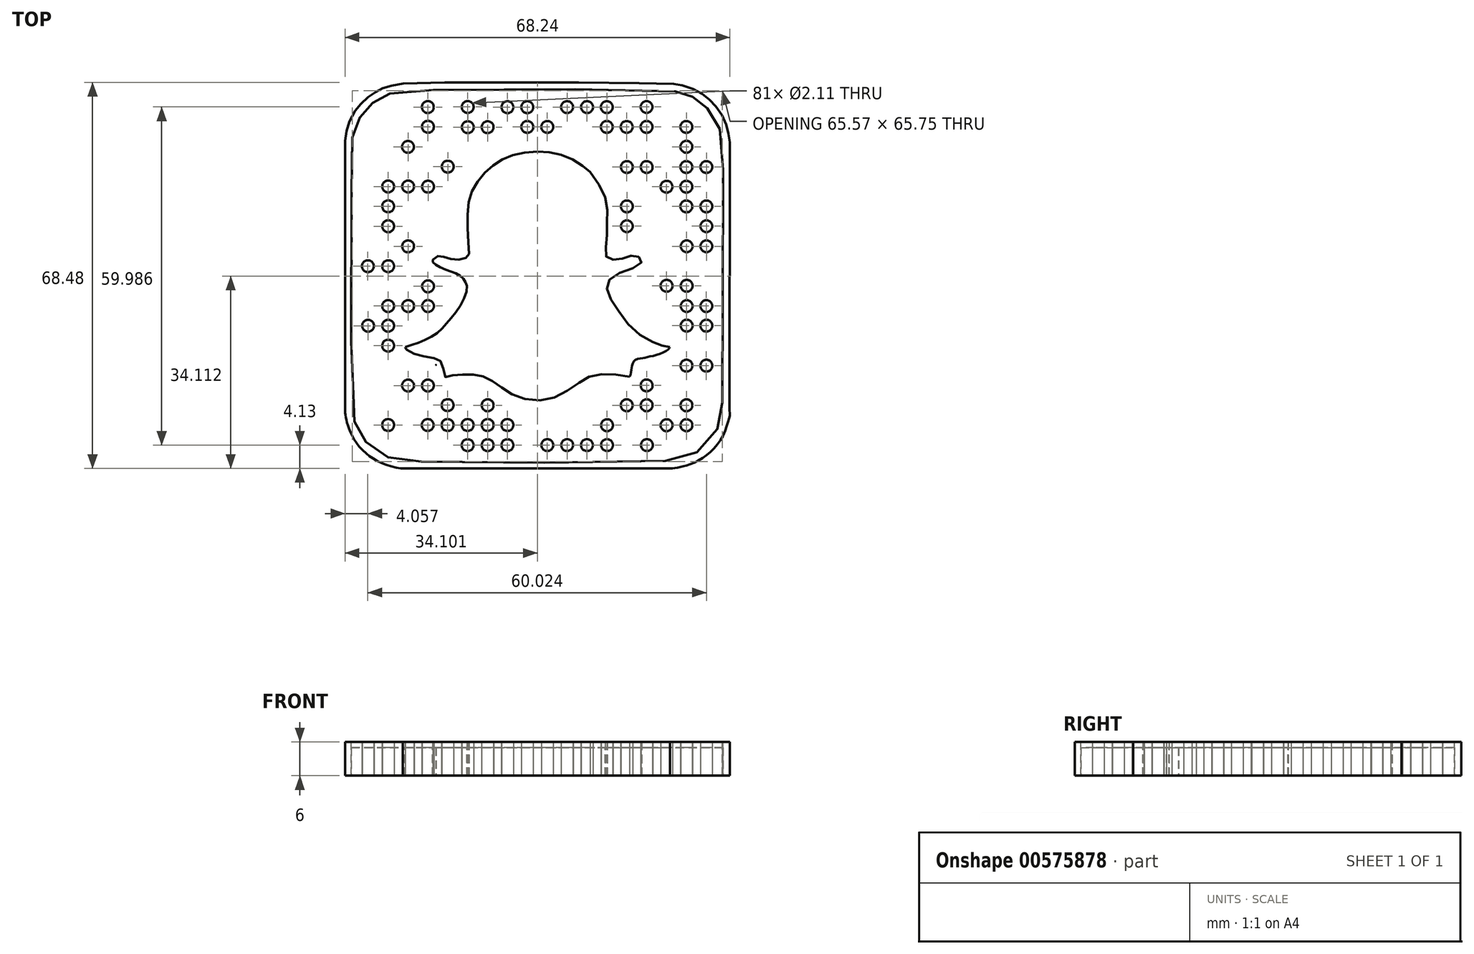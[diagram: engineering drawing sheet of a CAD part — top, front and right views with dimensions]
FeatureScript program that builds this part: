
annotation { "Feature Type Name" : "Feature", "Feature Type Description" : "" }
export const myFeature = defineFeature(function(context is Context, id is Id, definition is map)
    precondition{}
    {
        {
            var Q0;
            Q0=qCreatedBy(makeId("Top.planeOp"),FACE);
            var sketch = newSketch(context, id + "F0", { "sketchPlane" : qUnion([Q0])});
            skFitSpline(sketch, "E0", {"points": [v(0, 58.1) * mm, v(0, 10.12) * mm], "startDerivative": vector(0, -47.98) * mm, "endDerivative": vector(0, -47.98) * mm});
            skFitSpline(sketch, "E1", {"points": [v(0, 10.12) * mm, v(0.05, 9.95) * mm, v(0.07, 9.75) * mm, v(0.11, 9.43) * mm, v(0.2, 8.84) * mm, v(0.3, 8.4) * mm, v(0.46, 7.77) * mm, v(0.7, 7.06) * mm, v(1.15, 6.01) * mm, v(1.79, 4.9) * mm, v(2.7, 3.68) * mm, v(4, 2.48) * mm, v(4.96, 1.76) * mm, v(6.58, 0.92) * mm, v(8.37, 0.3) * mm, v(9.94, 0) * mm, v(10.25, 0) * mm], "startDerivative": vector(2.05, -5.87) * mm, "endDerivative": vector(6.58, 0.5) * mm});
            skFitSpline(sketch, "E2", {"points": [v(10.25, 0) * mm, v(57.62, 0) * mm], "startDerivative": vector(47.37, 0) * mm, "endDerivative": vector(47.37, 0) * mm});
            skFitSpline(sketch, "E3", {"points": [v(57.62, 0) * mm, v(58.24, 0) * mm, v(59.04, 0.17) * mm, v(59.98, 0.37) * mm, v(61.45, 0.82) * mm, v(63.58, 1.94) * mm, v(65.65, 3.77) * mm, v(67.27, 6.33) * mm, v(68, 8.6) * mm, v(68.24, 9.47) * mm, v(68.18, 10.3) * mm], "startDerivative": vector(9.32, -0.59) * mm, "endDerivative": vector(-1.36, 11.59) * mm});
            skFitSpline(sketch, "E4", {"points": [v(68.18, 10.3) * mm, v(68.22, 57.82) * mm, v(68.22, 57.86) * mm, v(68.22, 57.86) * mm], "startDerivative": vector(0.05, 72.45) * mm, "endDerivative": vector(0, 0.4) * mm});
            skFitSpline(sketch, "E5", {"points": [v(68.22, 57.86) * mm, v(68.04, 59.12) * mm, v(67.79, 60.34) * mm, v(67.15, 61.98) * mm, v(66.32, 63.49) * mm, v(65.2, 64.83) * mm, v(64.27, 65.75) * mm, v(63, 66.64) * mm, v(61.26, 67.48) * mm, v(59.55, 68.04) * mm, v(57.88, 68.22) * mm, v(9.78, 68.22) * mm, v(8.28, 67.9) * mm, v(6.86, 67.45) * mm, v(5.86, 66.99) * mm, v(4.83, 66.38) * mm, v(3.63, 65.49) * mm, v(2.59, 64.32) * mm, v(1.77, 63.32) * mm, v(0.67, 61.16) * mm, v(0.24, 59.69) * mm, v(0, 58.1) * mm], "startDerivative": vector(-5.16, 36.2) * mm, "endDerivative": vector(-5.3, -41.25) * mm});
            skFitSpline(sketch, "E6", {"points": [v(1.31, 58.65) * mm, v(1.3, 58.4) * mm, v(1.28, 58.1) * mm, v(1.42, 9.95) * mm, v(1.9, 7.9) * mm, v(2.76, 6.03) * mm, v(4.25, 4.07) * mm, v(6.21, 2.62) * mm, v(8.79, 1.5) * mm, v(11.56, 1.22) * mm, v(58.24, 1.44) * mm, v(61.22, 2.24) * mm, v(63.68, 3.77) * mm, v(65.85, 6.61) * mm, v(66.79, 9.3) * mm, v(66.89, 12.9) * mm, v(66.9, 57.86) * mm, v(66.64, 59.59) * mm, v(65.99, 61.46) * mm, v(64.89, 63.22) * mm, v(63.63, 64.5) * mm, v(63.04, 65.05) * mm, v(61.92, 65.75) * mm, v(60.43, 66.36) * mm, v(59.5, 66.63) * mm, v(57.98, 66.9) * mm, v(9.78, 66.93) * mm, v(8.5, 66.65) * mm, v(7.27, 66.2) * mm, v(5.9, 65.52) * mm, v(4.99, 64.9) * mm, v(4.16, 64.13) * mm, v(3.24, 63.17) * mm, v(2.3, 61.6) * mm, v(1.57, 59.77) * mm, v(1.31, 58.65) * mm]});
            skCircle(sketch, "E7", {"center": v(11.18, 57.03) * mm, "radius": 1.05 * mm});
            skCircle(sketch, "E8", {"center": v(14.71, 60.59) * mm, "radius": 1.05 * mm});
            skCircle(sketch, "E9", {"center": v(21.76, 64.1) * mm, "radius": 1.05 * mm});
            skCircle(sketch, "E10", {"center": v(21.79, 60.52) * mm, "radius": 1.05 * mm});
            skCircle(sketch, "E11", {"center": v(18.23, 53.52) * mm, "radius": 1.05 * mm});
            skCircle(sketch, "E12", {"center": v(14.74, 49.97) * mm, "radius": 1.05 * mm});
            skCircle(sketch, "E13", {"center": v(11.2, 50) * mm, "radius": 1.05 * mm});
            skCircle(sketch, "E14", {"center": v(14.7, 64.09) * mm, "radius": 1.05 * mm});
            skCircle(sketch, "E15", {"center": v(7.67, 46.48) * mm, "radius": 1.05 * mm});
            skCircle(sketch, "E16", {"center": v(7.67, 42.94) * mm, "radius": 1.05 * mm});
            skCircle(sketch, "E17", {"center": v(11.2, 39.38) * mm, "radius": 1.05 * mm});
            skCircle(sketch, "E18", {"center": v(7.67, 35.86) * mm, "radius": 1.05 * mm});
            skCircle(sketch, "E19", {"center": v(4.06, 35.86) * mm, "radius": 1.05 * mm});
            skCircle(sketch, "E20", {"center": v(7.67, 28.8) * mm, "radius": 1.05 * mm});
            skCircle(sketch, "E21", {"center": v(7.67, 25.3) * mm, "radius": 1.05 * mm});
            skCircle(sketch, "E22", {"center": v(7.67, 21.77) * mm, "radius": 1.05 * mm});
            skCircle(sketch, "E23", {"center": v(4.1, 25.3) * mm, "radius": 1.05 * mm});
            skCircle(sketch, "E24", {"center": v(14.73, 32.3) * mm, "radius": 1.05 * mm});
            skCircle(sketch, "E25", {"center": v(11.2, 28.8) * mm, "radius": 1.05 * mm});
            skCircle(sketch, "E26", {"center": v(14.73, 28.8) * mm, "radius": 1.05 * mm});
            skCircle(sketch, "E27", {"center": v(7.67, 50) * mm, "radius": 1.05 * mm});
            skCircle(sketch, "E28", {"center": v(14.68, 7.7) * mm, "radius": 1.05 * mm});
            skCircle(sketch, "E29", {"center": v(18.2, 7.7) * mm, "radius": 1.05 * mm});
            skCircle(sketch, "E30", {"center": v(25.3, 11.19) * mm, "radius": 1.05 * mm});
            skCircle(sketch, "E31", {"center": v(28.8, 7.7) * mm, "radius": 1.05 * mm});
            skCircle(sketch, "E32", {"center": v(25.3, 7.7) * mm, "radius": 1.05 * mm});
            skCircle(sketch, "E33", {"center": v(25.3, 4.12) * mm, "radius": 1.05 * mm});
            skCircle(sketch, "E34", {"center": v(18.2, 11.22) * mm, "radius": 1.05 * mm});
            skCircle(sketch, "E35", {"center": v(14.71, 14.7) * mm, "radius": 1.05 * mm});
            skCircle(sketch, "E36", {"center": v(11.2, 14.7) * mm, "radius": 1.05 * mm});
            skCircle(sketch, "E37", {"center": v(7.66, 7.7) * mm, "radius": 1.05 * mm});
            skCircle(sketch, "E38", {"center": v(21.75, 7.7) * mm, "radius": 1.05 * mm});
            skCircle(sketch, "E39", {"center": v(21.75, 4.12) * mm, "radius": 1.05 * mm});
            skCircle(sketch, "E40", {"center": v(46.46, 7.66) * mm, "radius": 1.05 * mm});
            skCircle(sketch, "E41", {"center": v(35.88, 4.13) * mm, "radius": 1.05 * mm});
            skCircle(sketch, "E42", {"center": v(28.8, 4.12) * mm, "radius": 1.05 * mm});
            skCircle(sketch, "E43", {"center": v(53.53, 4.13) * mm, "radius": 1.05 * mm});
            skCircle(sketch, "E44", {"center": v(42.9, 4.13) * mm, "radius": 1.05 * mm});
            skCircle(sketch, "E45", {"center": v(39.4, 4.13) * mm, "radius": 1.05 * mm});
            skCircle(sketch, "E46", {"center": v(46.46, 4.13) * mm, "radius": 1.05 * mm});
            skCircle(sketch, "E47", {"center": v(57.01, 7.66) * mm, "radius": 1.05 * mm});
            skCircle(sketch, "E48", {"center": v(53.48, 11.19) * mm, "radius": 1.05 * mm});
            skCircle(sketch, "E49", {"center": v(49.95, 11.19) * mm, "radius": 1.05 * mm});
            skCircle(sketch, "E50", {"center": v(64.07, 28.8) * mm, "radius": 1.05 * mm});
            skCircle(sketch, "E51", {"center": v(60.54, 18.22) * mm, "radius": 1.05 * mm});
            skCircle(sketch, "E52", {"center": v(64.06, 25.32) * mm, "radius": 1.05 * mm});
            skCircle(sketch, "E53", {"center": v(53.48, 14.72) * mm, "radius": 1.05 * mm});
            skCircle(sketch, "E54", {"center": v(60.54, 11.19) * mm, "radius": 1.05 * mm});
            skCircle(sketch, "E55", {"center": v(60.54, 7.66) * mm, "radius": 1.05 * mm});
            skCircle(sketch, "E56", {"center": v(60.58, 25.32) * mm, "radius": 1.05 * mm});
            skCircle(sketch, "E57", {"center": v(60.58, 28.8) * mm, "radius": 1.05 * mm});
            skCircle(sketch, "E58", {"center": v(64.06, 18.22) * mm, "radius": 1.05 * mm});
            skCircle(sketch, "E59", {"center": v(49.98, 46.46) * mm, "radius": 1.05 * mm});
            skCircle(sketch, "E60", {"center": v(60.58, 39.4) * mm, "radius": 1.05 * mm});
            skCircle(sketch, "E61", {"center": v(64.07, 39.4) * mm, "radius": 1.05 * mm});
            skCircle(sketch, "E62", {"center": v(57, 32.39) * mm, "radius": 1.05 * mm});
            skCircle(sketch, "E63", {"center": v(64.07, 42.96) * mm, "radius": 1.05 * mm});
            skCircle(sketch, "E64", {"center": v(60.58, 32.39) * mm, "radius": 1.05 * mm});
            skCircle(sketch, "E65", {"center": v(64.07, 46.46) * mm, "radius": 1.05 * mm});
            skCircle(sketch, "E66", {"center": v(60.53, 46.46) * mm, "radius": 1.05 * mm});
            skCircle(sketch, "E67", {"center": v(60.53, 57.04) * mm, "radius": 1.05 * mm});
            skCircle(sketch, "E68", {"center": v(60.53, 49.96) * mm, "radius": 1.05 * mm});
            skCircle(sketch, "E69", {"center": v(57, 49.96) * mm, "radius": 1.05 * mm});
            skCircle(sketch, "E70", {"center": v(60.53, 53.46) * mm, "radius": 1.05 * mm});
            skCircle(sketch, "E71", {"center": v(64.08, 53.46) * mm, "radius": 1.05 * mm});
            skCircle(sketch, "E72", {"center": v(53.5, 53.46) * mm, "radius": 1.05 * mm});
            skCircle(sketch, "E73", {"center": v(49.97, 53.46) * mm, "radius": 1.05 * mm});
            skCircle(sketch, "E74", {"center": v(49.98, 42.96) * mm, "radius": 1.05 * mm});
            skCircle(sketch, "E75", {"center": v(49.94, 60.56) * mm, "radius": 1.05 * mm});
            skCircle(sketch, "E76", {"center": v(53.47, 60.56) * mm, "radius": 1.05 * mm});
            skCircle(sketch, "E77", {"center": v(25.3, 60.52) * mm, "radius": 1.05 * mm});
            skCircle(sketch, "E78", {"center": v(32.34, 64.07) * mm, "radius": 1.05 * mm});
            skCircle(sketch, "E79", {"center": v(39.39, 64.08) * mm, "radius": 1.05 * mm});
            skCircle(sketch, "E80", {"center": v(46.42, 64.08) * mm, "radius": 1.05 * mm});
            skCircle(sketch, "E81", {"center": v(53.47, 64.1) * mm, "radius": 1.05 * mm});
            skCircle(sketch, "E82", {"center": v(46.42, 60.56) * mm, "radius": 1.05 * mm});
            skCircle(sketch, "E83", {"center": v(60.53, 60.56) * mm, "radius": 1.05 * mm});
            skCircle(sketch, "E84", {"center": v(28.8, 64.07) * mm, "radius": 1.05 * mm});
            skCircle(sketch, "E85", {"center": v(35.86, 60.56) * mm, "radius": 1.05 * mm});
            skCircle(sketch, "E86", {"center": v(42.92, 64.08) * mm, "radius": 1.05 * mm});
            skCircle(sketch, "E87", {"center": v(32.34, 60.56) * mm, "radius": 1.05 * mm});
            skFitSpline(sketch, "E88", {"points": [v(20.92, 38.22) * mm, v(20.74, 38.1) * mm, v(20.38, 38.01) * mm, v(19.53, 38.03) * mm, v(18.44, 38.3) * mm, v(17.73, 38.6) * mm, v(17.2, 38.75) * mm, v(16.43, 38.73) * mm, v(15.63, 38.49) * mm, v(15.09, 38.08) * mm, v(14.73, 37.65) * mm, v(14.55, 36.99) * mm, v(14.63, 36.18) * mm, v(15.53, 35.17) * mm, v(17, 34.5) * mm, v(18.57, 33.92) * mm, v(19.8, 33.42) * mm, v(20.47, 32.57) * mm, v(20.4, 31.38) * mm, v(19.8, 30.03) * mm, v(19.04, 28.66) * mm, v(17.54, 26.68) * mm, v(15.96, 25.15) * mm, v(14.12, 23.85) * mm, v(11.92, 22.93) * mm, v(10.85, 22.64) * mm, v(9.98, 22.41) * mm, v(9.5, 21.56) * mm, v(10.03, 20.41) * mm, v(11.46, 19.5) * mm, v(14.4, 18.73) * mm, v(16.12, 18.36) * mm, v(16.12, 18.32) * mm], "startDerivative": vector(-11.87, -10.02) * mm, "endDerivative": vector(-12.88, -22.9) * mm});
            skFitSpline(sketch, "E89", {"points": [v(16.12, 18.36) * mm, v(16.17, 18.29) * mm, v(16.22, 18.18) * mm, v(16.28, 17.97) * mm, v(16.39, 17.54) * mm, v(16.5, 17.06) * mm, v(16.63, 16.15) * mm, v(17.14, 15.44) * mm, v(18.08, 15.07) * mm, v(19.37, 15.35) * mm, v(20.56, 15.67) * mm, v(21.95, 15.65) * mm, v(23.55, 15.48) * mm, v(25.16, 14.84) * mm, v(26.44, 14.14) * mm, v(28.49, 12.72) * mm, v(30.12, 11.79) * mm, v(31.78, 11.26) * mm, v(33.93, 11.03) * mm, v(35.8, 11.14) * mm, v(37.84, 11.72) * mm, v(39.95, 12.8) * mm, v(41.25, 13.84) * mm, v(42.87, 14.75) * mm, v(44.7, 15.55) * mm, v(46.76, 15.62) * mm, v(48.87, 15.43) * mm, v(50.18, 15.24) * mm, v(51.1, 15.46) * mm, v(51.56, 16.38) * mm, v(51.8, 17.28) * mm, v(52.07, 18.35) * mm], "startDerivative": vector(5.86, -7.66) * mm, "endDerivative": vector(9.53, 30.18) * mm});
            skFitSpline(sketch, "E90", {"points": [v(51.97, 18.05) * mm, v(52.07, 18.36) * mm, v(53.1, 18.36) * mm, v(54.9, 18.76) * mm, v(57.23, 19.65) * mm, v(58.5, 20.77) * mm, v(58.77, 21.84) * mm, v(58.36, 22.37) * mm, v(57.52, 22.5) * mm, v(55.9, 23.08) * mm, v(53.74, 24.17) * mm, v(51.97, 25.38) * mm, v(50.52, 26.86) * mm, v(49.02, 28.9) * mm, v(48.12, 30.84) * mm, v(47.7, 31.97) * mm, v(48.2, 33.3) * mm, v(50.39, 34.2) * mm, v(52.57, 35.2) * mm, v(53.68, 36.32) * mm, v(53.5, 37.7) * mm, v(51.97, 38.76) * mm, v(50.41, 38.69) * mm, v(49.17, 38.3) * mm, v(47.85, 37.97) * mm, v(47.3, 38.42) * mm, v(47.38, 38.89) * mm, v(47.5, 46.78) * mm, v(46.64, 49.71) * mm, v(45.1, 52.28) * mm, v(43.08, 54.31) * mm, v(41.28, 55.54) * mm, v(38.35, 56.76) * mm, v(34.35, 57.22) * mm, v(31.46, 57.03) * mm, v(28.86, 56.35) * mm, v(26.5, 55.26) * mm, v(24.33, 53.59) * mm, v(22.3, 51.07) * mm, v(21.1, 48.42) * mm, v(20.76, 46.03) * mm, v(20.66, 42.86) * mm, v(20.78, 40.82) * mm, v(20.92, 38.22) * mm], "startDerivative": vector(-15.83, 66.6) * mm, "endDerivative": vector(5.1, -104.53) * mm});
            skFitSpline(sketch, "E91", {"points": [v(15.57, 36.99) * mm, v(15.57, 36.66) * mm, v(16.07, 36.13) * mm, v(17.82, 35.27) * mm, v(19.53, 34.67) * mm, v(20.72, 33.88) * mm, v(21.36, 33.06) * mm, v(21.63, 31.93) * mm, v(20.4, 28.76) * mm, v(18.25, 25.94) * mm, v(16.28, 23.97) * mm, v(13.6, 22.5) * mm, v(10.68, 21.51) * mm], "startDerivative": vector(-1.53, -9.27) * mm, "endDerivative": vector(-27.35, -8.3) * mm});
            skFitSpline(sketch, "E92", {"points": [v(10.68, 21.51) * mm, v(10.62, 21.47) * mm, v(10.68, 21.3) * mm, v(10.8, 21.14) * mm, v(11.65, 20.59) * mm, v(13.25, 20.05) * mm, v(15.04, 19.62) * mm, v(16.5, 19.42) * mm, v(17.03, 18.85) * mm, v(17.44, 17.86) * mm, v(17.75, 16.23) * mm, v(18.15, 16.3) * mm, v(19.53, 16.53) * mm, v(21.34, 16.66) * mm, v(23.4, 16.6) * mm, v(24.88, 16.18) * mm, v(26.79, 15.1) * mm, v(28.68, 13.7) * mm, v(31.44, 12.44) * mm, v(35.42, 12.14) * mm, v(38.84, 13.4) * mm, v(41.76, 15.35) * mm, v(43.77, 16.4) * mm, v(47.18, 16.68) * mm, v(50.43, 16.23) * mm], "startDerivative": vector(-9.2, -2.53) * mm, "endDerivative": vector(55.28, -9.82) * mm});
            skFitSpline(sketch, "E93", {"points": [v(50.43, 16.23) * mm, v(50.55, 16.43) * mm, v(50.72, 17.27) * mm, v(50.92, 18.28) * mm, v(51.42, 19.21) * mm, v(52.65, 19.54) * mm, v(53.8, 19.78) * mm, v(56, 20.37) * mm, v(57.45, 21.23) * mm, v(57.6, 21.5) * mm], "startDerivative": vector(2.35, 2.89) * mm, "endDerivative": vector(1.23, 4.14) * mm});
            skFitSpline(sketch, "E94", {"points": [v(57.6, 21.5) * mm, v(56.5, 21.74) * mm, v(54.94, 22.24) * mm, v(51.5, 24.28) * mm, v(48.5, 27.93) * mm, v(46.68, 30.92) * mm, v(46.53, 32.77) * mm, v(47.97, 34.37) * mm, v(51.3, 35.6) * mm, v(52.57, 36.6) * mm, v(52.3, 37.35) * mm, v(51.22, 37.81) * mm, v(49.91, 37.43) * mm, v(48.3, 37.05) * mm, v(46.76, 37.16) * mm, v(46.19, 37.86) * mm, v(46.37, 40.12) * mm, v(46.46, 42.85) * mm, v(46.5, 45.88) * mm, v(45.85, 48.87) * mm, v(43.45, 52.55) * mm], "startDerivative": vector(-30.34, 5.9) * mm, "endDerivative": vector(-38.13, 53.23) * mm});
            skFitSpline(sketch, "E95", {"points": [v(43.45, 52.55) * mm, v(42, 53.8) * mm, v(39.4, 55.23) * mm, v(36.64, 56) * mm, v(33.83, 56.2) * mm, v(30.61, 55.8) * mm, v(28.17, 54.93) * mm, v(26.1, 53.65) * mm, v(24.4, 52.02) * mm, v(22.86, 49.84) * mm, v(22, 47.63) * mm, v(21.75, 44.46) * mm, v(21.83, 40.72) * mm, v(21.96, 37.93) * mm, v(21.75, 37.51) * mm, v(21.06, 37.2) * mm, v(19.88, 37) * mm, v(18.7, 37.15) * mm, v(17.6, 37.5) * mm, v(16.97, 37.73) * mm, v(16.13, 37.51) * mm, v(15.57, 36.99) * mm], "startDerivative": vector(-27.46, 26.04) * mm, "endDerivative": vector(-16.2, -19.1) * mm});
            skSolve(sketch);
        }
        {
            var Q0;
            Q0 = qSketchRegion(id + "F0", true);
            extrude(context, id + "F1", {"entities" : qUnion([Q0]), "depth" : 5 * mm, "offsetDistance" : 25 * mm});
        }
        {
            var Q0;
            Q0 = qSketchRegion(id + "F0", true);
            var Q1;
            Q1=makeQuery(id+"F0.imprint","IMPRINT",FACE,{"disambiguationData":[TD([[makeQuery(id+"F0.imprint","IMPRINT",EDGE,{"derivedFrom":sQuery(id+"F0.wireOp",EDGE,"E91")}),1.0]])]});
            extrude(context, id + "F2", {"entities" : qUnion([Q0, Q1]), "operationType" : NewBodyOperationType.ADD, "depth" : 6 * mm, "offsetDistance" : 25 * mm});
        }
        {
            var Q0;
            Q0=makeQuery(id+"F0.imprint","IMPRINT",FACE,{"disambiguationData":[TD([[makeQuery(id+"F0.imprint","IMPRINT",EDGE,{"derivedFrom":sQuery(id+"F0.wireOp",EDGE,"E11")}),1.0]])]});
            var Q1;
            Q1=makeQuery(id+"F0.imprint","IMPRINT",FACE,{"disambiguationData":[TD([[makeQuery(id+"F0.imprint","IMPRINT",EDGE,{"derivedFrom":sQuery(id+"F0.wireOp",EDGE,"E12")}),1.0]])]});
            var Q2;
            Q2=makeQuery(id+"F0.imprint","IMPRINT",FACE,{"disambiguationData":[TD([[makeQuery(id+"F0.imprint","IMPRINT",EDGE,{"derivedFrom":sQuery(id+"F0.wireOp",EDGE,"E13")}),1.0]])]});
            var Q3;
            Q3=makeQuery(id+"F0.imprint","IMPRINT",FACE,{"disambiguationData":[TD([[makeQuery(id+"F0.imprint","IMPRINT",EDGE,{"derivedFrom":sQuery(id+"F0.wireOp",EDGE,"E27")}),1.0]])]});
            var Q4;
            Q4=makeQuery(id+"F0.imprint","IMPRINT",FACE,{"disambiguationData":[TD([[makeQuery(id+"F0.imprint","IMPRINT",EDGE,{"derivedFrom":sQuery(id+"F0.wireOp",EDGE,"E15")}),1.0]])]});
            var Q5;
            Q5=makeQuery(id+"F0.imprint","IMPRINT",FACE,{"disambiguationData":[TD([[makeQuery(id+"F0.imprint","IMPRINT",EDGE,{"derivedFrom":sQuery(id+"F0.wireOp",EDGE,"E16")}),1.0]])]});
            var Q6;
            Q6=makeQuery(id+"F0.imprint","IMPRINT",FACE,{"disambiguationData":[TD([[makeQuery(id+"F0.imprint","IMPRINT",EDGE,{"derivedFrom":sQuery(id+"F0.wireOp",EDGE,"E17")}),1.0]])]});
            var Q7;
            Q7=makeQuery(id+"F0.imprint","IMPRINT",FACE,{"disambiguationData":[TD([[makeQuery(id+"F0.imprint","IMPRINT",EDGE,{"derivedFrom":sQuery(id+"F0.wireOp",EDGE,"E7")}),1.0]])]});
            var Q8;
            Q8=makeQuery(id+"F0.imprint","IMPRINT",FACE,{"disambiguationData":[TD([[makeQuery(id+"F0.imprint","IMPRINT",EDGE,{"derivedFrom":sQuery(id+"F0.wireOp",EDGE,"E8")}),1.0]])]});
            var Q9;
            Q9=makeQuery(id+"F0.imprint","IMPRINT",FACE,{"disambiguationData":[TD([[makeQuery(id+"F0.imprint","IMPRINT",EDGE,{"derivedFrom":sQuery(id+"F0.wireOp",EDGE,"E14")}),1.0]])]});
            var Q10;
            Q10=makeQuery(id+"F0.imprint","IMPRINT",FACE,{"disambiguationData":[TD([[makeQuery(id+"F0.imprint","IMPRINT",EDGE,{"derivedFrom":sQuery(id+"F0.wireOp",EDGE,"E9")}),1.0]])]});
            var Q11;
            Q11=makeQuery(id+"F0.imprint","IMPRINT",FACE,{"disambiguationData":[TD([[makeQuery(id+"F0.imprint","IMPRINT",EDGE,{"derivedFrom":sQuery(id+"F0.wireOp",EDGE,"E10")}),1.0]])]});
            var Q12;
            Q12=makeQuery(id+"F0.imprint","IMPRINT",FACE,{"disambiguationData":[TD([[makeQuery(id+"F0.imprint","IMPRINT",EDGE,{"derivedFrom":sQuery(id+"F0.wireOp",EDGE,"E77")}),1.0]])]});
            var Q13;
            Q13=makeQuery(id+"F0.imprint","IMPRINT",FACE,{"disambiguationData":[TD([[makeQuery(id+"F0.imprint","IMPRINT",EDGE,{"derivedFrom":sQuery(id+"F0.wireOp",EDGE,"E84")}),1.0]])]});
            var Q14;
            Q14=makeQuery(id+"F0.imprint","IMPRINT",FACE,{"disambiguationData":[TD([[makeQuery(id+"F0.imprint","IMPRINT",EDGE,{"derivedFrom":sQuery(id+"F0.wireOp",EDGE,"E78")}),1.0]])]});
            var Q15;
            Q15=makeQuery(id+"F0.imprint","IMPRINT",FACE,{"disambiguationData":[TD([[makeQuery(id+"F0.imprint","IMPRINT",EDGE,{"derivedFrom":sQuery(id+"F0.wireOp",EDGE,"E87")}),1.0]])]});
            var Q16;
            Q16=makeQuery(id+"F0.imprint","IMPRINT",FACE,{"disambiguationData":[TD([[makeQuery(id+"F0.imprint","IMPRINT",EDGE,{"derivedFrom":sQuery(id+"F0.wireOp",EDGE,"E85")}),1.0]])]});
            var Q17;
            Q17=makeQuery(id+"F0.imprint","IMPRINT",FACE,{"disambiguationData":[TD([[makeQuery(id+"F0.imprint","IMPRINT",EDGE,{"derivedFrom":sQuery(id+"F0.wireOp",EDGE,"E79")}),1.0]])]});
            var Q18;
            Q18=makeQuery(id+"F0.imprint","IMPRINT",FACE,{"disambiguationData":[TD([[makeQuery(id+"F0.imprint","IMPRINT",EDGE,{"derivedFrom":sQuery(id+"F0.wireOp",EDGE,"E86")}),1.0]])]});
            var Q19;
            Q19=makeQuery(id+"F0.imprint","IMPRINT",FACE,{"disambiguationData":[TD([[makeQuery(id+"F0.imprint","IMPRINT",EDGE,{"derivedFrom":sQuery(id+"F0.wireOp",EDGE,"E80")}),1.0]])]});
            var Q20;
            Q20=makeQuery(id+"F0.imprint","IMPRINT",FACE,{"disambiguationData":[TD([[makeQuery(id+"F0.imprint","IMPRINT",EDGE,{"derivedFrom":sQuery(id+"F0.wireOp",EDGE,"E82")}),1.0]])]});
            var Q21;
            Q21=makeQuery(id+"F0.imprint","IMPRINT",FACE,{"disambiguationData":[TD([[makeQuery(id+"F0.imprint","IMPRINT",EDGE,{"derivedFrom":sQuery(id+"F0.wireOp",EDGE,"E75")}),1.0]])]});
            var Q22;
            Q22=makeQuery(id+"F0.imprint","IMPRINT",FACE,{"disambiguationData":[TD([[makeQuery(id+"F0.imprint","IMPRINT",EDGE,{"derivedFrom":sQuery(id+"F0.wireOp",EDGE,"E76")}),1.0]])]});
            var Q23;
            Q23=makeQuery(id+"F0.imprint","IMPRINT",FACE,{"disambiguationData":[TD([[makeQuery(id+"F0.imprint","IMPRINT",EDGE,{"derivedFrom":sQuery(id+"F0.wireOp",EDGE,"E81")}),1.0]])]});
            var Q24;
            Q24=makeQuery(id+"F0.imprint","IMPRINT",FACE,{"disambiguationData":[TD([[makeQuery(id+"F0.imprint","IMPRINT",EDGE,{"derivedFrom":sQuery(id+"F0.wireOp",EDGE,"E83")}),1.0]])]});
            var Q25;
            Q25=makeQuery(id+"F0.imprint","IMPRINT",FACE,{"disambiguationData":[TD([[makeQuery(id+"F0.imprint","IMPRINT",EDGE,{"derivedFrom":sQuery(id+"F0.wireOp",EDGE,"E67")}),1.0]])]});
            var Q26;
            Q26=makeQuery(id+"F0.imprint","IMPRINT",FACE,{"disambiguationData":[TD([[makeQuery(id+"F0.imprint","IMPRINT",EDGE,{"derivedFrom":sQuery(id+"F0.wireOp",EDGE,"E72")}),1.0]])]});
            var Q27;
            Q27=makeQuery(id+"F0.imprint","IMPRINT",FACE,{"disambiguationData":[TD([[makeQuery(id+"F0.imprint","IMPRINT",EDGE,{"derivedFrom":sQuery(id+"F0.wireOp",EDGE,"E73")}),1.0]])]});
            var Q28;
            Q28=makeQuery(id+"F0.imprint","IMPRINT",FACE,{"disambiguationData":[TD([[makeQuery(id+"F0.imprint","IMPRINT",EDGE,{"derivedFrom":sQuery(id+"F0.wireOp",EDGE,"E70")}),1.0]])]});
            var Q29;
            Q29=makeQuery(id+"F0.imprint","IMPRINT",FACE,{"disambiguationData":[TD([[makeQuery(id+"F0.imprint","IMPRINT",EDGE,{"derivedFrom":sQuery(id+"F0.wireOp",EDGE,"E71")}),1.0]])]});
            var Q30;
            Q30=makeQuery(id+"F0.imprint","IMPRINT",FACE,{"disambiguationData":[TD([[makeQuery(id+"F0.imprint","IMPRINT",EDGE,{"derivedFrom":sQuery(id+"F0.wireOp",EDGE,"E68")}),1.0]])]});
            var Q31;
            Q31=makeQuery(id+"F0.imprint","IMPRINT",FACE,{"disambiguationData":[TD([[makeQuery(id+"F0.imprint","IMPRINT",EDGE,{"derivedFrom":sQuery(id+"F0.wireOp",EDGE,"E69")}),1.0]])]});
            var Q32;
            Q32=makeQuery(id+"F0.imprint","IMPRINT",FACE,{"disambiguationData":[TD([[makeQuery(id+"F0.imprint","IMPRINT",EDGE,{"derivedFrom":sQuery(id+"F0.wireOp",EDGE,"E66")}),1.0]])]});
            var Q33;
            Q33=makeQuery(id+"F0.imprint","IMPRINT",FACE,{"disambiguationData":[TD([[makeQuery(id+"F0.imprint","IMPRINT",EDGE,{"derivedFrom":sQuery(id+"F0.wireOp",EDGE,"E65")}),1.0]])]});
            var Q34;
            Q34=makeQuery(id+"F0.imprint","IMPRINT",FACE,{"disambiguationData":[TD([[makeQuery(id+"F0.imprint","IMPRINT",EDGE,{"derivedFrom":sQuery(id+"F0.wireOp",EDGE,"E63")}),1.0]])]});
            var Q35;
            Q35=makeQuery(id+"F0.imprint","IMPRINT",FACE,{"disambiguationData":[TD([[makeQuery(id+"F0.imprint","IMPRINT",EDGE,{"derivedFrom":sQuery(id+"F0.wireOp",EDGE,"E61")}),1.0]])]});
            var Q36;
            Q36=makeQuery(id+"F0.imprint","IMPRINT",FACE,{"disambiguationData":[TD([[makeQuery(id+"F0.imprint","IMPRINT",EDGE,{"derivedFrom":sQuery(id+"F0.wireOp",EDGE,"E60")}),1.0]])]});
            var Q37;
            Q37=makeQuery(id+"F0.imprint","IMPRINT",FACE,{"disambiguationData":[TD([[makeQuery(id+"F0.imprint","IMPRINT",EDGE,{"derivedFrom":sQuery(id+"F0.wireOp",EDGE,"E74")}),1.0]])]});
            var Q38;
            Q38=makeQuery(id+"F0.imprint","IMPRINT",FACE,{"disambiguationData":[TD([[makeQuery(id+"F0.imprint","IMPRINT",EDGE,{"derivedFrom":sQuery(id+"F0.wireOp",EDGE,"E59")}),1.0]])]});
            var Q39;
            Q39=makeQuery(id+"F0.imprint","IMPRINT",FACE,{"disambiguationData":[TD([[makeQuery(id+"F0.imprint","IMPRINT",EDGE,{"derivedFrom":sQuery(id+"F0.wireOp",EDGE,"E62")}),1.0]])]});
            var Q40;
            Q40=makeQuery(id+"F0.imprint","IMPRINT",FACE,{"disambiguationData":[TD([[makeQuery(id+"F0.imprint","IMPRINT",EDGE,{"derivedFrom":sQuery(id+"F0.wireOp",EDGE,"E64")}),1.0]])]});
            var Q41;
            Q41=makeQuery(id+"F0.imprint","IMPRINT",FACE,{"disambiguationData":[TD([[makeQuery(id+"F0.imprint","IMPRINT",EDGE,{"derivedFrom":sQuery(id+"F0.wireOp",EDGE,"E57")}),1.0]])]});
            var Q42;
            Q42=makeQuery(id+"F0.imprint","IMPRINT",FACE,{"disambiguationData":[TD([[makeQuery(id+"F0.imprint","IMPRINT",EDGE,{"derivedFrom":sQuery(id+"F0.wireOp",EDGE,"E50")}),1.0]])]});
            var Q43;
            Q43=makeQuery(id+"F0.imprint","IMPRINT",FACE,{"disambiguationData":[TD([[makeQuery(id+"F0.imprint","IMPRINT",EDGE,{"derivedFrom":sQuery(id+"F0.wireOp",EDGE,"E52")}),1.0]])]});
            var Q44;
            Q44=makeQuery(id+"F0.imprint","IMPRINT",FACE,{"disambiguationData":[TD([[makeQuery(id+"F0.imprint","IMPRINT",EDGE,{"derivedFrom":sQuery(id+"F0.wireOp",EDGE,"E56")}),1.0]])]});
            var Q45;
            Q45=makeQuery(id+"F0.imprint","IMPRINT",FACE,{"disambiguationData":[TD([[makeQuery(id+"F0.imprint","IMPRINT",EDGE,{"derivedFrom":sQuery(id+"F0.wireOp",EDGE,"E51")}),1.0]])]});
            var Q46;
            Q46=makeQuery(id+"F0.imprint","IMPRINT",FACE,{"disambiguationData":[TD([[makeQuery(id+"F0.imprint","IMPRINT",EDGE,{"derivedFrom":sQuery(id+"F0.wireOp",EDGE,"E58")}),1.0]])]});
            var Q47;
            Q47=makeQuery(id+"F0.imprint","IMPRINT",FACE,{"disambiguationData":[TD([[makeQuery(id+"F0.imprint","IMPRINT",EDGE,{"derivedFrom":sQuery(id+"F0.wireOp",EDGE,"E54")}),1.0]])]});
            var Q48;
            Q48=makeQuery(id+"F0.imprint","IMPRINT",FACE,{"disambiguationData":[TD([[makeQuery(id+"F0.imprint","IMPRINT",EDGE,{"derivedFrom":sQuery(id+"F0.wireOp",EDGE,"E55")}),1.0]])]});
            var Q49;
            Q49=makeQuery(id+"F0.imprint","IMPRINT",FACE,{"disambiguationData":[TD([[makeQuery(id+"F0.imprint","IMPRINT",EDGE,{"derivedFrom":sQuery(id+"F0.wireOp",EDGE,"E47")}),1.0]])]});
            var Q50;
            Q50=makeQuery(id+"F0.imprint","IMPRINT",FACE,{"disambiguationData":[TD([[makeQuery(id+"F0.imprint","IMPRINT",EDGE,{"derivedFrom":sQuery(id+"F0.wireOp",EDGE,"E48")}),1.0]])]});
            var Q51;
            Q51=makeQuery(id+"F0.imprint","IMPRINT",FACE,{"disambiguationData":[TD([[makeQuery(id+"F0.imprint","IMPRINT",EDGE,{"derivedFrom":sQuery(id+"F0.wireOp",EDGE,"E53")}),1.0]])]});
            var Q52;
            Q52=makeQuery(id+"F0.imprint","IMPRINT",FACE,{"disambiguationData":[TD([[makeQuery(id+"F0.imprint","IMPRINT",EDGE,{"derivedFrom":sQuery(id+"F0.wireOp",EDGE,"E49")}),1.0]])]});
            var Q53;
            Q53=makeQuery(id+"F0.imprint","IMPRINT",FACE,{"disambiguationData":[TD([[makeQuery(id+"F0.imprint","IMPRINT",EDGE,{"derivedFrom":sQuery(id+"F0.wireOp",EDGE,"E40")}),1.0]])]});
            var Q54;
            Q54=makeQuery(id+"F0.imprint","IMPRINT",FACE,{"disambiguationData":[TD([[makeQuery(id+"F0.imprint","IMPRINT",EDGE,{"derivedFrom":sQuery(id+"F0.wireOp",EDGE,"E46")}),1.0]])]});
            var Q55;
            Q55=makeQuery(id+"F0.imprint","IMPRINT",FACE,{"disambiguationData":[TD([[makeQuery(id+"F0.imprint","IMPRINT",EDGE,{"derivedFrom":sQuery(id+"F0.wireOp",EDGE,"E43")}),1.0]])]});
            var Q56;
            Q56=makeQuery(id+"F0.imprint","IMPRINT",FACE,{"disambiguationData":[TD([[makeQuery(id+"F0.imprint","IMPRINT",EDGE,{"derivedFrom":sQuery(id+"F0.wireOp",EDGE,"E44")}),1.0]])]});
            var Q57;
            Q57=makeQuery(id+"F0.imprint","IMPRINT",FACE,{"disambiguationData":[TD([[makeQuery(id+"F0.imprint","IMPRINT",EDGE,{"derivedFrom":sQuery(id+"F0.wireOp",EDGE,"E45")}),1.0]])]});
            var Q58;
            Q58=makeQuery(id+"F0.imprint","IMPRINT",FACE,{"disambiguationData":[TD([[makeQuery(id+"F0.imprint","IMPRINT",EDGE,{"derivedFrom":sQuery(id+"F0.wireOp",EDGE,"E41")}),1.0]])]});
            var Q59;
            Q59=makeQuery(id+"F0.imprint","IMPRINT",FACE,{"disambiguationData":[TD([[makeQuery(id+"F0.imprint","IMPRINT",EDGE,{"derivedFrom":sQuery(id+"F0.wireOp",EDGE,"E42")}),1.0]])]});
            var Q60;
            Q60=makeQuery(id+"F0.imprint","IMPRINT",FACE,{"disambiguationData":[TD([[makeQuery(id+"F0.imprint","IMPRINT",EDGE,{"derivedFrom":sQuery(id+"F0.wireOp",EDGE,"E31")}),1.0]])]});
            var Q61;
            Q61=makeQuery(id+"F0.imprint","IMPRINT",FACE,{"disambiguationData":[TD([[makeQuery(id+"F0.imprint","IMPRINT",EDGE,{"derivedFrom":sQuery(id+"F0.wireOp",EDGE,"E32")}),1.0]])]});
            var Q62;
            Q62=makeQuery(id+"F0.imprint","IMPRINT",FACE,{"disambiguationData":[TD([[makeQuery(id+"F0.imprint","IMPRINT",EDGE,{"derivedFrom":sQuery(id+"F0.wireOp",EDGE,"E30")}),1.0]])]});
            var Q63;
            Q63=makeQuery(id+"F0.imprint","IMPRINT",FACE,{"disambiguationData":[TD([[makeQuery(id+"F0.imprint","IMPRINT",EDGE,{"derivedFrom":sQuery(id+"F0.wireOp",EDGE,"E33")}),1.0]])]});
            var Q64;
            Q64=makeQuery(id+"F0.imprint","IMPRINT",FACE,{"disambiguationData":[TD([[makeQuery(id+"F0.imprint","IMPRINT",EDGE,{"derivedFrom":sQuery(id+"F0.wireOp",EDGE,"E39")}),1.0]])]});
            var Q65;
            Q65=makeQuery(id+"F0.imprint","IMPRINT",FACE,{"disambiguationData":[TD([[makeQuery(id+"F0.imprint","IMPRINT",EDGE,{"derivedFrom":sQuery(id+"F0.wireOp",EDGE,"E38")}),1.0]])]});
            var Q66;
            Q66=makeQuery(id+"F0.imprint","IMPRINT",FACE,{"disambiguationData":[TD([[makeQuery(id+"F0.imprint","IMPRINT",EDGE,{"derivedFrom":sQuery(id+"F0.wireOp",EDGE,"E29")}),1.0]])]});
            var Q67;
            Q67=makeQuery(id+"F0.imprint","IMPRINT",FACE,{"disambiguationData":[TD([[makeQuery(id+"F0.imprint","IMPRINT",EDGE,{"derivedFrom":sQuery(id+"F0.wireOp",EDGE,"E28")}),1.0]])]});
            var Q68;
            Q68=makeQuery(id+"F0.imprint","IMPRINT",FACE,{"disambiguationData":[TD([[makeQuery(id+"F0.imprint","IMPRINT",EDGE,{"derivedFrom":sQuery(id+"F0.wireOp",EDGE,"E34")}),1.0]])]});
            var Q69;
            Q69=makeQuery(id+"F0.imprint","IMPRINT",FACE,{"disambiguationData":[TD([[makeQuery(id+"F0.imprint","IMPRINT",EDGE,{"derivedFrom":sQuery(id+"F0.wireOp",EDGE,"E37")}),1.0]])]});
            var Q70;
            Q70=makeQuery(id+"F0.imprint","IMPRINT",FACE,{"disambiguationData":[TD([[makeQuery(id+"F0.imprint","IMPRINT",EDGE,{"derivedFrom":sQuery(id+"F0.wireOp",EDGE,"E36")}),1.0]])]});
            var Q71;
            Q71=makeQuery(id+"F0.imprint","IMPRINT",FACE,{"disambiguationData":[TD([[makeQuery(id+"F0.imprint","IMPRINT",EDGE,{"derivedFrom":sQuery(id+"F0.wireOp",EDGE,"E35")}),1.0]])]});
            var Q72;
            Q72=makeQuery(id+"F0.imprint","IMPRINT",FACE,{"disambiguationData":[TD([[makeQuery(id+"F0.imprint","IMPRINT",EDGE,{"derivedFrom":sQuery(id+"F0.wireOp",EDGE,"E22")}),1.0]])]});
            var Q73;
            Q73=makeQuery(id+"F0.imprint","IMPRINT",FACE,{"disambiguationData":[TD([[makeQuery(id+"F0.imprint","IMPRINT",EDGE,{"derivedFrom":sQuery(id+"F0.wireOp",EDGE,"E21")}),1.0]])]});
            var Q74;
            Q74=makeQuery(id+"F0.imprint","IMPRINT",FACE,{"disambiguationData":[TD([[makeQuery(id+"F0.imprint","IMPRINT",EDGE,{"derivedFrom":sQuery(id+"F0.wireOp",EDGE,"E23")}),1.0]])]});
            var Q75;
            Q75=makeQuery(id+"F0.imprint","IMPRINT",FACE,{"disambiguationData":[TD([[makeQuery(id+"F0.imprint","IMPRINT",EDGE,{"derivedFrom":sQuery(id+"F0.wireOp",EDGE,"E20")}),1.0]])]});
            var Q76;
            Q76=makeQuery(id+"F0.imprint","IMPRINT",FACE,{"disambiguationData":[TD([[makeQuery(id+"F0.imprint","IMPRINT",EDGE,{"derivedFrom":sQuery(id+"F0.wireOp",EDGE,"E25")}),1.0]])]});
            var Q77;
            Q77=makeQuery(id+"F0.imprint","IMPRINT",FACE,{"disambiguationData":[TD([[makeQuery(id+"F0.imprint","IMPRINT",EDGE,{"derivedFrom":sQuery(id+"F0.wireOp",EDGE,"E26")}),1.0]])]});
            var Q78;
            Q78=makeQuery(id+"F0.imprint","IMPRINT",FACE,{"disambiguationData":[TD([[makeQuery(id+"F0.imprint","IMPRINT",EDGE,{"derivedFrom":sQuery(id+"F0.wireOp",EDGE,"E24")}),1.0]])]});
            var Q79;
            Q79=makeQuery(id+"F0.imprint","IMPRINT",FACE,{"disambiguationData":[TD([[makeQuery(id+"F0.imprint","IMPRINT",EDGE,{"derivedFrom":sQuery(id+"F0.wireOp",EDGE,"E18")}),1.0]])]});
            var Q80;
            Q80=makeQuery(id+"F0.imprint","IMPRINT",FACE,{"disambiguationData":[TD([[makeQuery(id+"F0.imprint","IMPRINT",EDGE,{"derivedFrom":sQuery(id+"F0.wireOp",EDGE,"E19")}),1.0]])]});
            extrude(context, id + "F3", {"entities" : qUnion([Q0, Q1, Q2, Q3, Q4, Q5, Q6, Q7, Q8, Q9, Q10, Q11, Q12, Q13, Q14, Q15, Q16, Q17, Q18, Q19, Q20, Q21, Q22, Q23, Q24, Q25, Q26, Q27, Q28, Q29, Q30, Q31, Q32, Q33, Q34, Q35, Q36, Q37, Q38, Q39, Q40, Q41, Q42, Q43, Q44, Q45, Q46, Q47, Q48, Q49, Q50, Q51, Q52, Q53, Q54, Q55, Q56, Q57, Q58, Q59, Q60, Q61, Q62, Q63, Q64, Q65, Q66, Q67, Q68, Q69, Q70, Q71, Q72, Q73, Q74, Q75, Q76, Q77, Q78, Q79, Q80]), "depth" : 6 * mm, "offsetDistance" : 25 * mm});
        }
        {
            var Q0;
            Q0=makeQuery(id+"F0.imprint","IMPRINT",FACE,{"disambiguationData":[TD([[makeQuery(id+"F0.imprint","IMPRINT",EDGE,{"derivedFrom":sQuery(id+"F0.wireOp",EDGE,"E6")}),1.0]])]});
            extrude(context, id + "F4", {"entities" : qUnion([Q0]), "depth" : 5 * mm, "offsetDistance" : 25 * mm});
        }
    });
